# Revit family: Bath-Feet-KALLISTA-Circle-P50203
name_source: partatom
category: Plumbing Fixtures
units: mm (PartAtom-declared; Revit-internal decimal feet)

## family parameters
Cut with Voids When Loaded = No
Host = Face
Maintain Annotation Orientation = No
OmniClass Number = 23.31.15.00
OmniClass Title = Bathtubs
Part Type = Normal
Room Calculation Point = No
Round Connector Dimension = Use Diameter
Shared = No

## types (6) — shared parameters
ADA Compliant = No
Assembly Code = D2010500
CW Connection = Yes
Cold Water Inlet = Cold Water Inlet
Date Modified = 06/17/2025
Default Elevation = 0"
Description = Cast Iron Feet
Drain Included = No
HW Connection = Yes
Height = 14 13/16"
Hot Water Inlet = Hot Water Inlet
Length = 11 3/8"
Manufacturer = Kallista Co.
Master Format 2014 = 22 41 19
Master Format 2014 Name = Residential Bathtubs
Material = Cast Iron
Product Documentation Link = https://techcomm.kohler.com
Product Name = Circle
URL = https://www.kallista.com
Vent Connection = Yes
Waste Connection = Yes
Waste Water Outlet = Waste Water Outlet
WaterSense Certified = No
Width = 5 15/16"

## per-type parameters (varying)
| type | Finish | Model | Product Page URL | Type |
| 0-White | Kallista-Cast_Iron-0-White | P50203-00-0 |  | 1 |
| AD-Nickel Silver | Kallista-Cast Iron-AD-Nickel_Silver | P50203-00-AD | https://www.kallista.com | 2 |
| CP-Polished Chrome | KALLISTA-Cast_Iron-CP-Polished_Chrome | P50203-00-CP | https://www.kallista.com | 3 |
| NA-Prime | Kallista-Cast_Iron-NA-Prime | P50203-00-NA | https://www.kallista.com | 4 |
| P5-Iron Black | Kallista-Cast_Iron-P5-Iron_Black | P50203-00-P5 | https://www.kallista.com | 5 |
| W-White | Kallista-Cast_Iron-0-White | P50203-00-W | https://www.kallista.com | 6 |

## geometry (parser evidence)
native form markers: Sweep x6
no freeform markers — native parametric forms only
